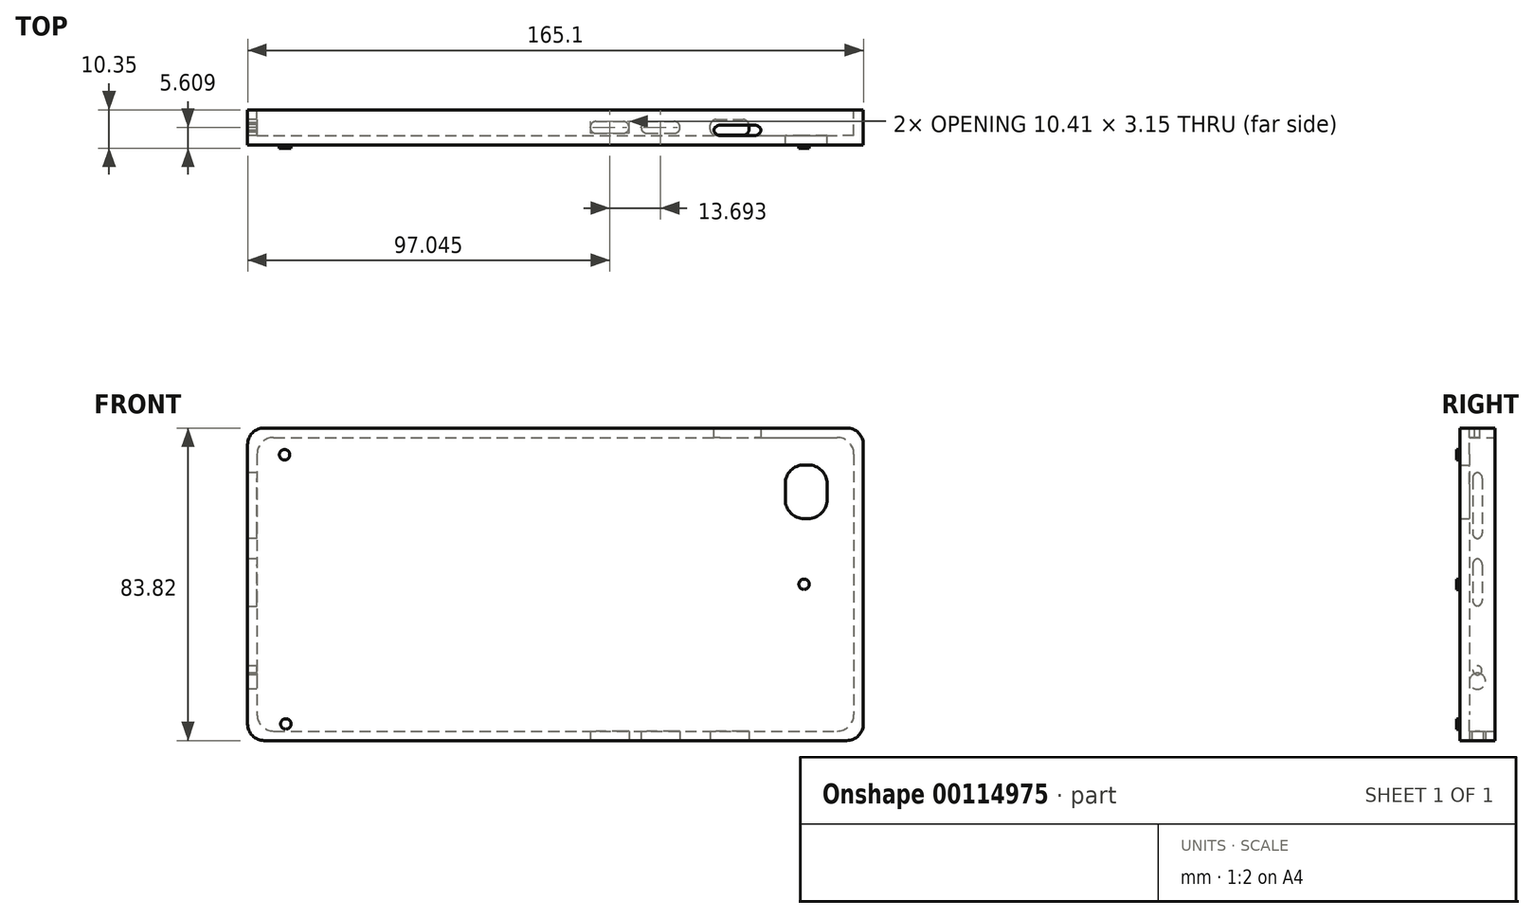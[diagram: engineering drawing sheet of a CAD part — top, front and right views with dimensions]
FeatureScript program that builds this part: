
annotation { "Feature Type Name" : "Feature", "Feature Type Description" : "" }
export const myFeature = defineFeature(function(context is Context, id is Id, definition is map)
    precondition{}
    {
        {
            var Q0;
            Q0=qCreatedBy(makeId("Front.planeOp"),FACE);
            var sketch = newSketch(context, id + "F0", { "sketchPlane" : qUnion([Q0])});
            skPoint(sketch, "E0.start.orphan", {"position": v(-132.9, 0) * mm});
            skLineSegment(sketch, "E1.top", {"start": v(-80.52, -39.85) * mm, "end": v(79.5, -39.85) * mm});
            skLineSegment(sketch, "E1.left", {"start": v(-80.52, 38.9) * mm, "end": v(-80.52, -39.85) * mm});
            skLineSegment(sketch, "E1.right", {"start": v(79.5, 38.9) * mm, "end": v(79.5, -39.85) * mm});
            skLineSegment(sketch, "E2", {"start": v(-80.52, 38.9) * mm, "end": v(79.5, 38.9) * mm});
            skSolve(sketch);
        }
        {
            var Q0;
            Q0=makeQuery(id+"F0.imprint","IMPRINT",FACE,{"disambiguationData":[TD([[makeQuery(id+"F0.imprint","IMPRINT",EDGE,{"derivedFrom":sQuery(id+"F0.wireOp",EDGE,"E1.top")}),1.0]])]});
            extrude(context, id + "F1", {"entities" : qUnion([Q0]), "depth" : 6.94 * mm});
        }
        {
            var Q0;
            Q0=makeQuery(id+"F1.opExtrude","CAP_FACE",FACE,{"disambiguationData":[OSD([sQuery(id+"F0.wireOp",EDGE,"E1.top"),sQuery(id+"F0.wireOp",EDGE,"E1.left"),sQuery(id+"F0.wireOp",EDGE,"E1.right"),sQuery(id+"F0.wireOp",EDGE,"E2")])],"isStart":true});
            var Q1;
            Q1=makeQuery(id+"F1.opExtrude","SWEPT_BODY",BODY,{"disambiguationData":[OSD([sQuery(id+"F0.wireOp",EDGE,"E1.top"),sQuery(id+"F0.wireOp",EDGE,"E1.left"),sQuery(id+"F0.wireOp",EDGE,"E1.right"),sQuery(id+"F0.wireOp",EDGE,"E2")])]});
            shell(context, id + "F2", {"entities" : qUnion([Q0]), "parts" : qUnion([Q1]), "thickness" : 2.54 * mm, "oppositeDirection" : true});
        }
        {
            var Q0;
            Q0=makeQuery(id+"F1.opExtrude","SWEPT_EDGE",EDGE,{"disambiguationData":[OSD([sQuery(id+"F0.wireOp",EDGE,"E1.left"),sQuery(id+"F0.wireOp",EDGE,"E2")])]});
            var Q1;
            Q1=makeQuery(id+"F1.opExtrude","SWEPT_EDGE",EDGE,{"disambiguationData":[OSD([sQuery(id+"F0.wireOp",EDGE,"E1.top"),sQuery(id+"F0.wireOp",EDGE,"E1.left")])]});
            var Q2;
            Q2=makeQuery(id+"F1.opExtrude","SWEPT_EDGE",EDGE,{"disambiguationData":[OSD([sQuery(id+"F0.wireOp",EDGE,"E1.top"),sQuery(id+"F0.wireOp",EDGE,"E1.right")])]});
            var Q3;
            Q3=makeQuery(id+"F2.opShell","OFFSET_EDGE",EDGE,{"disambiguationData":[OSD([sQuery(id+"F0.wireOp",EDGE,"E1.right"),sQuery(id+"F0.wireOp",EDGE,"E2")])]});
            var Q4;
            Q4=makeQuery(id+"F1.opExtrude","SWEPT_EDGE",EDGE,{"disambiguationData":[OSD([sQuery(id+"F0.wireOp",EDGE,"E1.right"),sQuery(id+"F0.wireOp",EDGE,"E2")])]});
            var Q5;
            Q5=makeQuery(id+"F2.opShell","OFFSET_EDGE",EDGE,{"disambiguationData":[OSD([sQuery(id+"F0.wireOp",EDGE,"E1.top"),sQuery(id+"F0.wireOp",EDGE,"E1.right")])]});
            var Q6;
            Q6=makeQuery(id+"F2.opShell","OFFSET_EDGE",EDGE,{"disambiguationData":[OSD([sQuery(id+"F0.wireOp",EDGE,"E1.top"),sQuery(id+"F0.wireOp",EDGE,"E1.left")])]});
            var Q7;
            Q7=makeQuery(id+"F2.opShell","OFFSET_EDGE",EDGE,{"disambiguationData":[OSD([sQuery(id+"F0.wireOp",EDGE,"E1.left"),sQuery(id+"F0.wireOp",EDGE,"E2")])]});
            fillet(context, id + "F3", {"entities" : qUnion([Q0, Q1, Q2, Q3, Q4, Q5, Q6, Q7]), "radius" : 4.44 * mm, "tangentPropagation" : true, "allowEdgeOverflow" : false});
        }
        {
            var Q0;
            Q0=makeQuery(id+"F2.opShell","OFFSET_FACE",FACE,{"disambiguationData":[OSD([sQuery(id+"F0.wireOp",EDGE,"E1.top"),sQuery(id+"F0.wireOp",EDGE,"E1.left"),sQuery(id+"F0.wireOp",EDGE,"E1.right"),sQuery(id+"F0.wireOp",EDGE,"E2")])]});
            var sketch = newSketch(context, id + "F4", { "sketchPlane" : qUnion([Q0])});
            skLineSegment(sketch, "E3", {"start": v(-72.3, 31.53) * mm, "end": v(-72.3, 17.12) * mm});
            skLineSegment(sketch, "E4", {"start": v(-72.3, 31.53) * mm, "end": v(-61.1, 31.53) * mm});
            skLineSegment(sketch, "E5", {"start": v(-72.3, 17.12) * mm, "end": v(-61.1, 17.12) * mm});
            skLineSegment(sketch, "E6", {"start": v(-61.1, 17.12) * mm, "end": v(-61.1, 31.53) * mm});
            skSolve(sketch);
        }
        {
            var Q0;
            Q0=makeQuery(id+"F1.opExtrude","SWEPT_FACE",FACE,{"disambiguationData":[OSD([sQuery(id+"F0.wireOp",EDGE,"E2")])]});
            var sketch = newSketch(context, id + "F5", { "sketchPlane" : qUnion([Q0])});
            skSolve(sketch);
        }
        {
            var Q0;
            Q0 = qSketchRegion(id + "F4", true);
            extrude(context, id + "F6", {"entities" : qUnion([Q0]), "operationType" : NewBodyOperationType.REMOVE, "oppositeDirection" : true, "depth" : 25.4 * mm});
        }
        {
            var Q0;
            Q0=makeQuery(id+"F6.boolean.opBoolean","COPY",EDGE,{"derivedFrom":makeQuery(id+"F6.opExtrude","SWEPT_EDGE",EDGE,{"disambiguationData":[OSD([sQuery(id+"F4.wireOp",EDGE,"E3"),sQuery(id+"F4.wireOp",EDGE,"E4")])]})});
            var Q1;
            Q1=makeQuery(id+"F6.boolean.opBoolean","COPY",EDGE,{"derivedFrom":makeQuery(id+"F6.opExtrude","SWEPT_EDGE",EDGE,{"disambiguationData":[OSD([sQuery(id+"F4.wireOp",EDGE,"E3"),sQuery(id+"F4.wireOp",EDGE,"E5")])]})});
            var Q2;
            Q2=makeQuery(id+"F6.boolean.opBoolean","COPY",EDGE,{"derivedFrom":makeQuery(id+"F6.opExtrude","SWEPT_EDGE",EDGE,{"disambiguationData":[OSD([sQuery(id+"F4.wireOp",EDGE,"E4"),sQuery(id+"F4.wireOp",EDGE,"E6")])]})});
            var Q3;
            Q3=makeQuery(id+"F6.boolean.opBoolean","COPY",EDGE,{"derivedFrom":makeQuery(id+"F6.opExtrude","SWEPT_EDGE",EDGE,{"disambiguationData":[OSD([sQuery(id+"F4.wireOp",EDGE,"E5"),sQuery(id+"F4.wireOp",EDGE,"E6")])]})});
            fillet(context, id + "F7", {"entities" : qUnion([Q0, Q1, Q2, Q3]), "radius" : 5.08 * mm, "tangentPropagation" : true, "allowEdgeOverflow" : false});
        }
        {
            var Q0;
            Q0=makeQuery(id+"F1.opExtrude","SWEPT_FACE",FACE,{"disambiguationData":[OSD([sQuery(id+"F0.wireOp",EDGE,"E1.left")])]});
            var sketch = newSketch(context, id + "F8", { "sketchPlane" : qUnion([Q0])});
            skLineSegment(sketch, "E7", {"start": v(4.74, -37.94) * mm, "end": v(4.74, 36.99) * mm, "construction": true});
            skLineSegment(sketch, "E8.bottom", {"start": v(6.01, 6.35) * mm, "end": v(3.47, 6.35) * mm});
            skLineSegment(sketch, "E8.top", {"start": v(6.01, -6.35) * mm, "end": v(3.47, -6.35) * mm});
            skLineSegment(sketch, "E8.left", {"start": v(6.01, 6.35) * mm, "end": v(6.01, -6.35) * mm});
            skLineSegment(sketch, "E8.right", {"start": v(3.47, 6.35) * mm, "end": v(3.47, -6.35) * mm});
            skPoint(sketch, "E8.middle", {"position": v(4.74, 0) * mm});
            skLineSegment(sketch, "E9.bottom", {"start": v(6.01, 29.5) * mm, "end": v(3.47, 29.5) * mm});
            skLineSegment(sketch, "E9.top", {"start": v(6.01, 11.71) * mm, "end": v(3.47, 11.71) * mm});
            skLineSegment(sketch, "E9.left", {"start": v(6.01, 29.5) * mm, "end": v(6.01, 11.71) * mm});
            skLineSegment(sketch, "E9.right", {"start": v(3.47, 29.5) * mm, "end": v(3.47, 11.71) * mm});
            skPoint(sketch, "E9.middle", {"position": v(4.74, 20.6) * mm});
            skCircle(sketch, "E10", {"center": v(4.74, -26.47) * mm, "radius": 2.16 * mm});
            skCircle(sketch, "E11", {"center": v(4.74, -23.56) * mm, "radius": 1.2 * mm});
            skSolve(sketch);
        }
        {
            var Q0;
            {var subQ0=sQuery(id+"F8.wireOp",EDGE,"E11");var subQ1=sQuery(id+"F8.wireOp",EDGE,"E10");var subQ2=makeQuery(id+"F8.imprint","INTERSECT",VERTEX,{"disambiguationData":[OD(0.0)],"derivedFrom":[subQ1,subQ0]});Q0=makeQuery(id+"F8.imprint","IMPRINT",FACE,{"disambiguationData":[TD([[makeQuery(id+"F8.imprint","IMPRINT",EDGE,{"disambiguationData":[TD([[subQ2,1.0]])],"derivedFrom":subQ1}),1.0]])]});}
            var Q1;
            {var subQ0=sQuery(id+"F8.wireOp",EDGE,"E11");var subQ1=sQuery(id+"F8.wireOp",EDGE,"E10");var subQ2=makeQuery(id+"F8.imprint","INTERSECT",VERTEX,{"disambiguationData":[OD(0.0)],"derivedFrom":[subQ1,subQ0]});Q1=makeQuery(id+"F8.imprint","IMPRINT",FACE,{"disambiguationData":[TD([[makeQuery(id+"F8.imprint","IMPRINT",EDGE,{"disambiguationData":[TD([[subQ2,-1.0]])],"derivedFrom":subQ1}),-1.0]])]});}
            var Q2;
            Q2=makeQuery(id+"F8.imprint","IMPRINT",FACE,{"disambiguationData":[TD([[makeQuery(id+"F8.imprint","IMPRINT",EDGE,{"derivedFrom":sQuery(id+"F8.wireOp",EDGE,"E8.bottom")}),1.0]])]});
            var Q3;
            Q3=makeQuery(id+"F8.imprint","IMPRINT",FACE,{"disambiguationData":[TD([[makeQuery(id+"F8.imprint","IMPRINT",EDGE,{"derivedFrom":sQuery(id+"F8.wireOp",EDGE,"E9.bottom")}),1.0]])]});
            extrude(context, id + "F9", {"entities" : qUnion([Q0, Q1, Q2, Q3]), "operationType" : NewBodyOperationType.REMOVE, "oppositeDirection" : true, "depth" : 25.4 * mm});
        }
        {
            var Q0;
            Q0=makeQuery(id+"F1.opExtrude","SWEPT_FACE",FACE,{"disambiguationData":[OSD([sQuery(id+"F0.wireOp",EDGE,"E1.top")])]});
            var sketch = newSketch(context, id + "F10", { "sketchPlane" : qUnion([Q0])});
            skLineSegment(sketch, "E12", {"start": v(77.6, 4.74) * mm, "end": v(-78.62, 4.74) * mm, "construction": true});
            skLineSegment(sketch, "E13.bottom", {"start": v(40.98, 6.85) * mm, "end": v(51.34, 6.85) * mm});
            skLineSegment(sketch, "E13.top", {"start": v(40.98, 2.63) * mm, "end": v(51.34, 2.63) * mm});
            skLineSegment(sketch, "E13.left", {"start": v(40.98, 6.85) * mm, "end": v(40.98, 2.63) * mm});
            skLineSegment(sketch, "E13.right", {"start": v(51.34, 6.85) * mm, "end": v(51.34, 2.63) * mm});
            skPoint(sketch, "E13.middle", {"position": v(46.16, 4.74) * mm});
            skLineSegment(sketch, "E14.bottom", {"start": v(22.47, 6.32) * mm, "end": v(32.89, 6.32) * mm});
            skLineSegment(sketch, "E14.top", {"start": v(22.47, 3.17) * mm, "end": v(32.89, 3.17) * mm});
            skLineSegment(sketch, "E14.left", {"start": v(22.47, 6.32) * mm, "end": v(22.47, 3.17) * mm});
            skLineSegment(sketch, "E14.right", {"start": v(32.89, 6.32) * mm, "end": v(32.89, 3.17) * mm});
            skPoint(sketch, "E14.middle", {"position": v(27.68, 4.74) * mm});
            skLineSegment(sketch, "E15.bottom", {"start": v(8.78, 6.32) * mm, "end": v(19.2, 6.32) * mm});
            skLineSegment(sketch, "E15.top", {"start": v(8.78, 3.17) * mm, "end": v(19.2, 3.17) * mm});
            skLineSegment(sketch, "E15.left", {"start": v(8.78, 6.32) * mm, "end": v(8.78, 3.17) * mm});
            skLineSegment(sketch, "E15.right", {"start": v(19.2, 6.32) * mm, "end": v(19.2, 3.17) * mm});
            skPoint(sketch, "E15.middle", {"position": v(13.99, 4.74) * mm});
            skSolve(sketch);
        }
        {
            var Q0;
            Q0 = qSketchRegion(id + "F10", true);
            extrude(context, id + "F11", {"entities" : qUnion([Q0]), "operationType" : NewBodyOperationType.REMOVE, "oppositeDirection" : true, "depth" : 25.4 * mm});
        }
        {
            var Q0;
            Q0=makeQuery(id+"F11.boolean.opBoolean","COPY",EDGE,{"derivedFrom":makeQuery(id+"F11.opExtrude","SWEPT_EDGE",EDGE,{"disambiguationData":[OSD([sQuery(id+"F10.wireOp",EDGE,"E15.bottom"),sQuery(id+"F10.wireOp",EDGE,"E15.right")])]})});
            var Q1;
            Q1=makeQuery(id+"F11.boolean.opBoolean","COPY",EDGE,{"derivedFrom":makeQuery(id+"F11.opExtrude","SWEPT_EDGE",EDGE,{"disambiguationData":[OSD([sQuery(id+"F10.wireOp",EDGE,"E15.bottom"),sQuery(id+"F10.wireOp",EDGE,"E15.left")])]})});
            var Q2;
            Q2=makeQuery(id+"F11.boolean.opBoolean","COPY",EDGE,{"derivedFrom":makeQuery(id+"F11.opExtrude","SWEPT_EDGE",EDGE,{"disambiguationData":[OSD([sQuery(id+"F10.wireOp",EDGE,"E15.top"),sQuery(id+"F10.wireOp",EDGE,"E15.left")])]})});
            var Q3;
            Q3=makeQuery(id+"F11.boolean.opBoolean","COPY",EDGE,{"derivedFrom":makeQuery(id+"F11.opExtrude","SWEPT_EDGE",EDGE,{"disambiguationData":[OSD([sQuery(id+"F10.wireOp",EDGE,"E15.top"),sQuery(id+"F10.wireOp",EDGE,"E15.right")])]})});
            var Q4;
            Q4=makeQuery(id+"F11.boolean.opBoolean","COPY",EDGE,{"derivedFrom":makeQuery(id+"F11.opExtrude","SWEPT_EDGE",EDGE,{"disambiguationData":[OSD([sQuery(id+"F10.wireOp",EDGE,"E14.bottom"),sQuery(id+"F10.wireOp",EDGE,"E14.right")])]})});
            var Q5;
            Q5=makeQuery(id+"F11.boolean.opBoolean","COPY",EDGE,{"derivedFrom":makeQuery(id+"F11.opExtrude","SWEPT_EDGE",EDGE,{"disambiguationData":[OSD([sQuery(id+"F10.wireOp",EDGE,"E14.top"),sQuery(id+"F10.wireOp",EDGE,"E14.right")])]})});
            var Q6;
            Q6=makeQuery(id+"F11.boolean.opBoolean","COPY",EDGE,{"derivedFrom":makeQuery(id+"F11.opExtrude","SWEPT_EDGE",EDGE,{"disambiguationData":[OSD([sQuery(id+"F10.wireOp",EDGE,"E14.bottom"),sQuery(id+"F10.wireOp",EDGE,"E14.left")])]})});
            var Q7;
            Q7=makeQuery(id+"F11.boolean.opBoolean","COPY",EDGE,{"derivedFrom":makeQuery(id+"F11.opExtrude","SWEPT_EDGE",EDGE,{"disambiguationData":[OSD([sQuery(id+"F10.wireOp",EDGE,"E14.top"),sQuery(id+"F10.wireOp",EDGE,"E14.left")])]})});
            var Q8;
            Q8=makeQuery(id+"F11.boolean.opBoolean","COPY",EDGE,{"derivedFrom":makeQuery(id+"F11.opExtrude","SWEPT_EDGE",EDGE,{"disambiguationData":[OSD([sQuery(id+"F10.wireOp",EDGE,"E13.top"),sQuery(id+"F10.wireOp",EDGE,"E13.right")])]})});
            var Q9;
            Q9=makeQuery(id+"F11.boolean.opBoolean","COPY",EDGE,{"derivedFrom":makeQuery(id+"F11.opExtrude","SWEPT_EDGE",EDGE,{"disambiguationData":[OSD([sQuery(id+"F10.wireOp",EDGE,"E13.bottom"),sQuery(id+"F10.wireOp",EDGE,"E13.right")])]})});
            var Q10;
            Q10=makeQuery(id+"F11.boolean.opBoolean","COPY",EDGE,{"derivedFrom":makeQuery(id+"F11.opExtrude","SWEPT_EDGE",EDGE,{"disambiguationData":[OSD([sQuery(id+"F10.wireOp",EDGE,"E13.bottom"),sQuery(id+"F10.wireOp",EDGE,"E13.left")])]})});
            var Q11;
            Q11=makeQuery(id+"F11.boolean.opBoolean","COPY",EDGE,{"derivedFrom":makeQuery(id+"F11.opExtrude","SWEPT_EDGE",EDGE,{"disambiguationData":[OSD([sQuery(id+"F10.wireOp",EDGE,"E13.top"),sQuery(id+"F10.wireOp",EDGE,"E13.left")])]})});
            var Q12;
            Q12=makeQuery(id+"F9.boolean.opBoolean","COPY",EDGE,{"derivedFrom":makeQuery(id+"F9.opExtrude","SWEPT_EDGE",EDGE,{"disambiguationData":[OSD([sQuery(id+"F8.wireOp",EDGE,"E9.top"),sQuery(id+"F8.wireOp",EDGE,"E9.right")])]})});
            var Q13;
            Q13=makeQuery(id+"F9.boolean.opBoolean","COPY",EDGE,{"derivedFrom":makeQuery(id+"F9.opExtrude","SWEPT_EDGE",EDGE,{"disambiguationData":[OSD([sQuery(id+"F8.wireOp",EDGE,"E9.bottom"),sQuery(id+"F8.wireOp",EDGE,"E9.left")])]})});
            var Q14;
            Q14=makeQuery(id+"F9.boolean.opBoolean","COPY",EDGE,{"derivedFrom":makeQuery(id+"F9.opExtrude","SWEPT_EDGE",EDGE,{"disambiguationData":[OSD([sQuery(id+"F8.wireOp",EDGE,"E9.bottom"),sQuery(id+"F8.wireOp",EDGE,"E9.right")])]})});
            var Q15;
            Q15=makeQuery(id+"F9.boolean.opBoolean","COPY",EDGE,{"derivedFrom":makeQuery(id+"F9.opExtrude","SWEPT_EDGE",EDGE,{"disambiguationData":[OSD([sQuery(id+"F8.wireOp",EDGE,"E9.top"),sQuery(id+"F8.wireOp",EDGE,"E9.left")])]})});
            var Q16;
            Q16=makeQuery(id+"F9.boolean.opBoolean","COPY",EDGE,{"derivedFrom":makeQuery(id+"F9.opExtrude","SWEPT_EDGE",EDGE,{"disambiguationData":[OSD([sQuery(id+"F8.wireOp",EDGE,"E8.bottom"),sQuery(id+"F8.wireOp",EDGE,"E8.left")])]})});
            var Q17;
            Q17=makeQuery(id+"F9.boolean.opBoolean","COPY",EDGE,{"derivedFrom":makeQuery(id+"F9.opExtrude","SWEPT_EDGE",EDGE,{"disambiguationData":[OSD([sQuery(id+"F8.wireOp",EDGE,"E8.top"),sQuery(id+"F8.wireOp",EDGE,"E8.left")])]})});
            var Q18;
            Q18=makeQuery(id+"F9.boolean.opBoolean","COPY",EDGE,{"derivedFrom":makeQuery(id+"F9.opExtrude","SWEPT_EDGE",EDGE,{"disambiguationData":[OSD([sQuery(id+"F8.wireOp",EDGE,"E8.top"),sQuery(id+"F8.wireOp",EDGE,"E8.right")])]})});
            var Q19;
            Q19=makeQuery(id+"F9.boolean.opBoolean","COPY",EDGE,{"derivedFrom":makeQuery(id+"F9.opExtrude","SWEPT_EDGE",EDGE,{"disambiguationData":[OSD([sQuery(id+"F8.wireOp",EDGE,"E8.bottom"),sQuery(id+"F8.wireOp",EDGE,"E8.right")])]})});
            fillet(context, id + "F12", {"entities" : qUnion([Q0, Q1, Q2, Q3, Q4, Q5, Q6, Q7, Q8, Q9, Q10, Q11, Q12, Q13, Q14, Q15, Q16, Q17, Q18, Q19]), "radius" : 1.53 * mm, "tangentPropagation" : true, "allowEdgeOverflow" : false});
        }
        {
            var Q0;
            {var subQ0=sQuery(id+"F0.wireOp",EDGE,"E2");Q0=makeQuery(id+"F5.imprint","IMPRINT",FACE,{"disambiguationData":[TD([[makeQuery(id+"F5.imprint","IMPRINT",EDGE,{"derivedFrom":makeQuery(id+"F1.opExtrude","CAP_EDGE",EDGE,{"disambiguationData":[OSD([subQ0])],"isStart":true})}),-1.0]])]});}
            var sketch = newSketch(context, id + "F13", { "sketchPlane" : qUnion([Q0])});
            skLineSegment(sketch, "E16.bottom", {"start": v(41.91, -4.09) * mm, "end": v(54.61, -4.09) * mm});
            skLineSegment(sketch, "E16.top", {"start": v(41.91, -6.93) * mm, "end": v(54.61, -6.93) * mm});
            skLineSegment(sketch, "E16.left", {"start": v(41.91, -4.09) * mm, "end": v(41.91, -6.93) * mm});
            skLineSegment(sketch, "E16.right", {"start": v(54.61, -4.09) * mm, "end": v(54.61, -6.93) * mm});
            skSolve(sketch);
        }
        {
            var Q0;
            Q0 = qSketchRegion(id + "F13", true);
            extrude(context, id + "F14", {"entities" : qUnion([Q0]), "operationType" : NewBodyOperationType.REMOVE, "oppositeDirection" : true, "depth" : 25.4 * mm});
        }
        {
            var Q0;
            Q0=makeQuery(id+"F14.boolean.opBoolean","COPY",EDGE,{"derivedFrom":makeQuery(id+"F14.opExtrude","SWEPT_EDGE",EDGE,{"disambiguationData":[OSD([sQuery(id+"F13.wireOp",EDGE,"E16.bottom"),sQuery(id+"F13.wireOp",EDGE,"E16.right")])]})});
            var Q1;
            Q1=makeQuery(id+"F14.boolean.opBoolean","COPY",EDGE,{"derivedFrom":makeQuery(id+"F14.opExtrude","SWEPT_EDGE",EDGE,{"disambiguationData":[OSD([sQuery(id+"F13.wireOp",EDGE,"E16.bottom"),sQuery(id+"F13.wireOp",EDGE,"E16.left")])]})});
            var Q2;
            Q2=makeQuery(id+"F14.boolean.opBoolean","COPY",EDGE,{"derivedFrom":makeQuery(id+"F14.opExtrude","SWEPT_EDGE",EDGE,{"disambiguationData":[OSD([sQuery(id+"F13.wireOp",EDGE,"E16.top"),sQuery(id+"F13.wireOp",EDGE,"E16.right")])]})});
            var Q3;
            Q3=makeQuery(id+"F14.boolean.opBoolean","COPY",EDGE,{"derivedFrom":makeQuery(id+"F14.opExtrude","SWEPT_EDGE",EDGE,{"disambiguationData":[OSD([sQuery(id+"F13.wireOp",EDGE,"E16.top"),sQuery(id+"F13.wireOp",EDGE,"E16.left")])]})});
            fillet(context, id + "F15", {"entities" : qUnion([Q0, Q1, Q2, Q3]), "radius" : 1.76 * mm, "tangentPropagation" : true, "allowEdgeOverflow" : false});
        }
        {
            var Q0;
            Q0=makeQuery(id+"F1.opExtrude","CAP_FACE",FACE,{"disambiguationData":[OSD([sQuery(id+"F0.wireOp",EDGE,"E1.top"),sQuery(id+"F0.wireOp",EDGE,"E1.left"),sQuery(id+"F0.wireOp",EDGE,"E1.right"),sQuery(id+"F0.wireOp",EDGE,"E2")])],"isStart":false});
            var sketch = newSketch(context, id + "F16", { "sketchPlane" : qUnion([Q0])});
            skCircle(sketch, "E17", {"center": v(66.15, -0.48) * mm, "radius": 1.4 * mm});
            skPoint(sketch, "E17.centerSnap0", {"position": v(82.04, -0.48) * mm});
            skCircle(sketch, "E18", {"center": v(-73.16, 34.24) * mm, "radius": 1.4 * mm});
            skCircle(sketch, "E19", {"center": v(-72.8, -37.94) * mm, "radius": 1.4 * mm});
            skSolve(sketch);
        }
        {
            var Q0;
            Q0=makeQuery(id+"F16.imprint","IMPRINT",FACE,{"disambiguationData":[TD([[makeQuery(id+"F16.imprint","IMPRINT",EDGE,{"derivedFrom":sQuery(id+"F16.wireOp",EDGE,"E17")}),1.0]])]});
            var Q1;
            Q1=makeQuery(id+"F16.imprint","IMPRINT",FACE,{"disambiguationData":[TD([[makeQuery(id+"F16.imprint","IMPRINT",EDGE,{"derivedFrom":sQuery(id+"F16.wireOp",EDGE,"E18")}),1.0]])]});
            var Q2;
            Q2=makeQuery(id+"F16.imprint","IMPRINT",FACE,{"disambiguationData":[TD([[makeQuery(id+"F16.imprint","IMPRINT",EDGE,{"derivedFrom":sQuery(id+"F16.wireOp",EDGE,"E19")}),1.0]])]});
            extrude(context, id + "F17", {"entities" : qUnion([Q0, Q1, Q2]), "operationType" : NewBodyOperationType.ADD, "depth" : 0.87 * mm});
        }
    });
